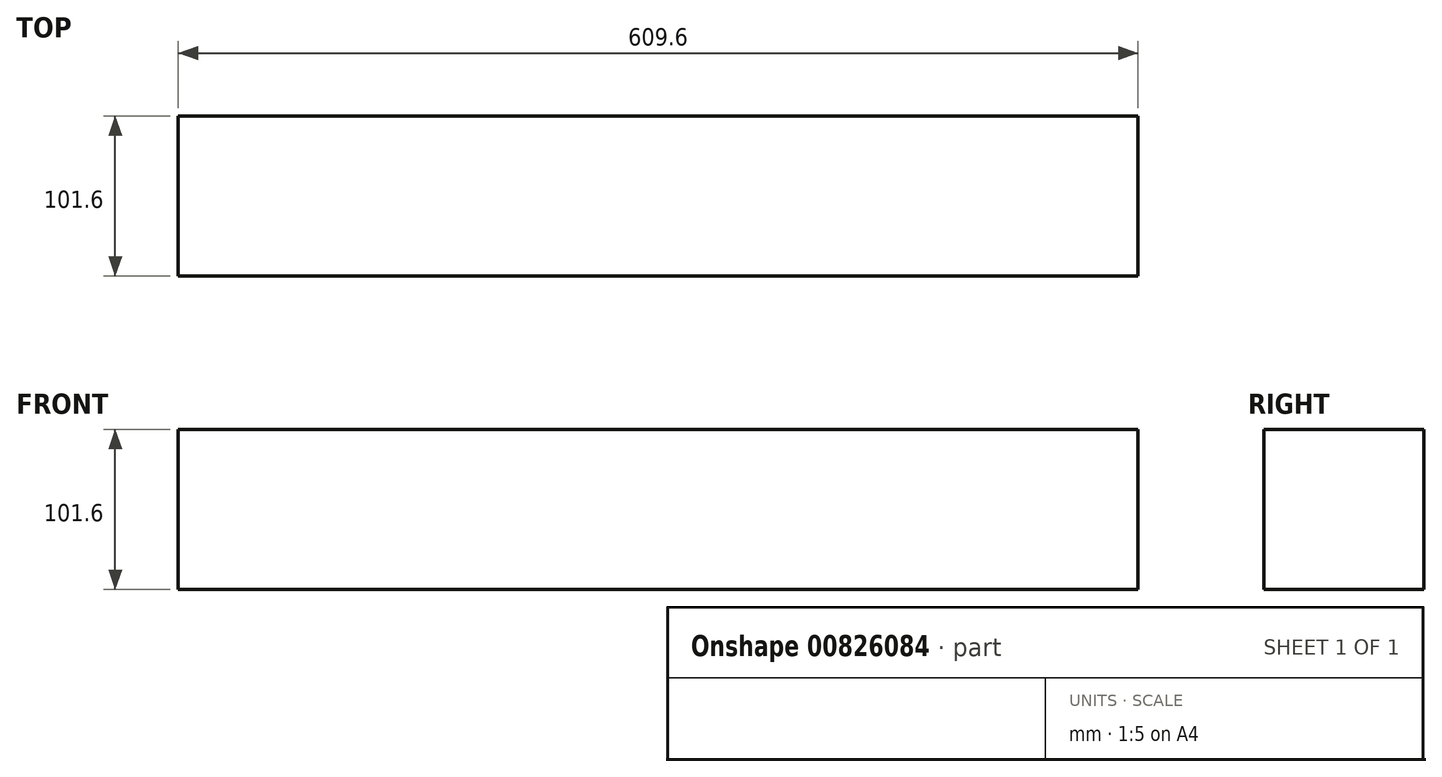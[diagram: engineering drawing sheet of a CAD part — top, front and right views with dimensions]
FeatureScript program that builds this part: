
annotation { "Feature Type Name" : "Feature", "Feature Type Description" : "" }
export const myFeature = defineFeature(function(context is Context, id is Id, definition is map)
    precondition{}
    {
        {
            var Q0;
            Q0=qCreatedBy(makeId("Right.planeOp"),FACE);
            var sketch = newSketch(context, id + "F0", { "sketchPlane" : qUnion([Q0])});
            skLineSegment(sketch, "E0.bottom", {"start": v(0, 0) * mm, "end": v(101.6, 0) * mm});
            skLineSegment(sketch, "E0.top", {"start": v(0, 101.6) * mm, "end": v(101.6, 101.6) * mm});
            skLineSegment(sketch, "E0.left", {"start": v(0, 0) * mm, "end": v(0, 101.6) * mm});
            skLineSegment(sketch, "E0.right", {"start": v(101.6, 0) * mm, "end": v(101.6, 101.6) * mm});
            skSolve(sketch);
        }
        {
            var Q0;
            Q0 = qSketchRegion(id + "F0", true);
            extrude(context, id + "F1", {"entities" : qUnion([Q0]), "depth" : 609.6 * mm, "offsetDistance" : 25 * mm});
        }
    });
